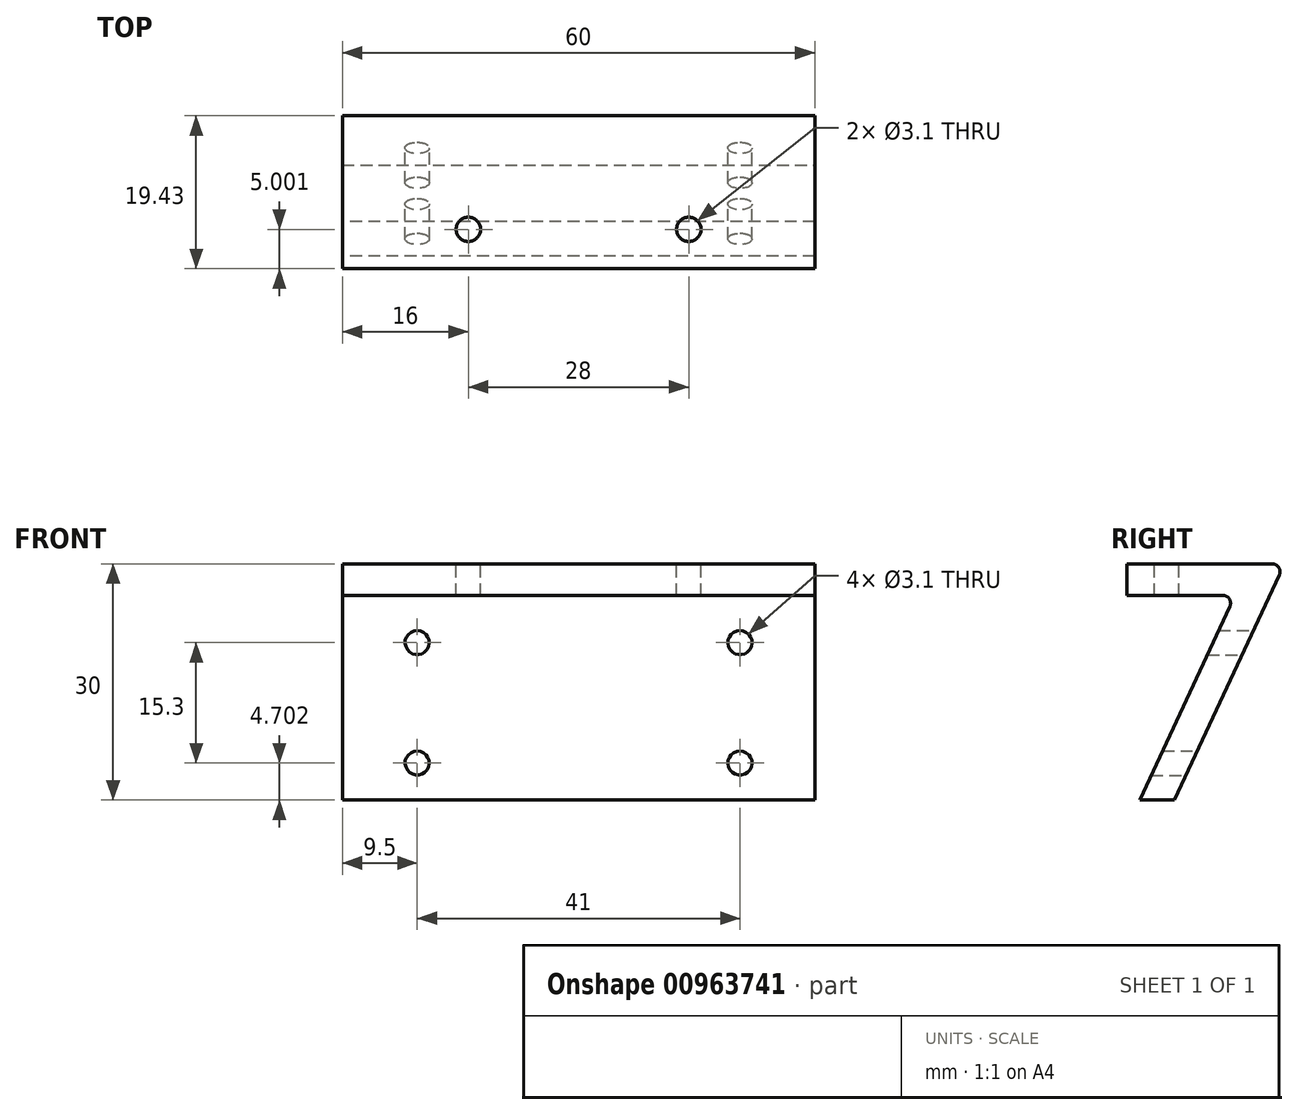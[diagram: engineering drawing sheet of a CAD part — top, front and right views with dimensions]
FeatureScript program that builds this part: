
annotation { "Feature Type Name" : "Feature", "Feature Type Description" : "" }
export const myFeature = defineFeature(function(context is Context, id is Id, definition is map)
    precondition{}
    {
        {
            var Q0;
            Q0=qCreatedBy(makeId("Right.planeOp"),FACE);
            var sketch = newSketch(context, id + "F0", { "sketchPlane" : qUnion([Q0])});
            skLineSegment(sketch, "E0", {"start": v(-23.5, -2.28) * mm, "end": v(-3.5, -2.28) * mm});
            skLineSegment(sketch, "E1", {"start": v(-3.5, -2.28) * mm, "end": v(-17.49, -32.28) * mm});
            skLineSegment(sketch, "E2.0", {"start": v(-9.78, -6.28) * mm, "end": v(-21.9, -32.28) * mm});
            skLineSegment(sketch, "E2.1", {"start": v(-23.5, -6.28) * mm, "end": v(-9.78, -6.28) * mm});
            skLineSegment(sketch, "E3", {"start": v(-23.5, -2.28) * mm, "end": v(-23.5, -6.28) * mm});
            skLineSegment(sketch, "E4", {"start": v(-21.9, -32.28) * mm, "end": v(-17.49, -32.28) * mm});
            skSolve(sketch);
        }
        {
            var Q0;
            Q0=makeQuery(id+"F0.imprint","IMPRINT",FACE,{"disambiguationData":[TD([[makeQuery(id+"F0.imprint","IMPRINT",EDGE,{"derivedFrom":sQuery(id+"F0.wireOp",EDGE,"E0")}),-1.0]])]});
            extrude(context, id + "F1", {"entities" : qUnion([Q0]), "depth" : 60 * mm, "offsetDistance" : 25 * mm});
        }
        {
            var Q0;
            Q0=qCreatedBy(makeId("Top.planeOp"),FACE);
            var sketch = newSketch(context, id + "F2", { "sketchPlane" : qUnion([Q0])});
            skCircle(sketch, "E5", {"center": v(16, -18.5) * mm, "radius": 1.5 * mm});
            skCircle(sketch, "E6", {"center": v(44, -18.5) * mm, "radius": 1.5 * mm});
            skSolve(sketch);
        }
        {
            var Q0;
            Q0=qCreatedBy(makeId("Front.planeOp"),FACE);
            var sketch = newSketch(context, id + "F3", { "sketchPlane" : qUnion([Q0])});
            skCircle(sketch, "E7", {"center": v(9.5, -12.28) * mm, "radius": 1.55 * mm});
            skCircle(sketch, "E8", {"center": v(50.5, -12.28) * mm, "radius": 1.55 * mm});
            skCircle(sketch, "E9", {"center": v(9.5, -27.58) * mm, "radius": 1.55 * mm});
            skCircle(sketch, "E10", {"center": v(50.5, -27.58) * mm, "radius": 1.55 * mm});
            skSolve(sketch);
        }
        {
            var Q0;
            Q0=sQuery(id+"F3.wireOp",VERTEX,"E8.center");
            var Q1;
            Q1=sQuery(id+"F3.wireOp",VERTEX,"E7.center");
            var Q2;
            Q2=sQuery(id+"F3.wireOp",VERTEX,"E9.center");
            var Q3;
            Q3=sQuery(id+"F3.wireOp",VERTEX,"E10.center");
            var Q4;
            Q4=makeQuery(id+"F1.opExtrude","SWEPT_BODY",BODY,{"disambiguationData":[OSD([sQuery(id+"F0.wireOp",EDGE,"E0"),sQuery(id+"F0.wireOp",EDGE,"E1"),sQuery(id+"F0.wireOp",EDGE,"E2.0"),sQuery(id+"F0.wireOp",EDGE,"E2.1"),sQuery(id+"F0.wireOp",EDGE,"E3"),sQuery(id+"F0.wireOp",EDGE,"E4")])]});
            hole(context, id + "F4", {"style" : HoleStyle.SIMPLE, "endStyle" : HoleEndStyle.THROUGH, "oppositeDirection" : true, "holeDiameter" : 3.1 * mm, "majorDiameter" : 5 * mm, "isTappedThrough" : true, "tappedDepth" : 12 * mm, "tapClearance" : 3, "locations" : qUnion([Q0, Q1, Q2, Q3]), "scope" : qUnion([Q4])});
        }
        {
            var Q0;
            Q0=sQuery(id+"F2.wireOp",VERTEX,"E5.center");
            var Q1;
            Q1=sQuery(id+"F2.wireOp",VERTEX,"E6.center");
            var Q2;
            Q2=makeQuery(id+"F1.opExtrude","SWEPT_BODY",BODY,{"disambiguationData":[OSD([sQuery(id+"F0.wireOp",EDGE,"E0"),sQuery(id+"F0.wireOp",EDGE,"E1"),sQuery(id+"F0.wireOp",EDGE,"E2.0"),sQuery(id+"F0.wireOp",EDGE,"E2.1"),sQuery(id+"F0.wireOp",EDGE,"E3"),sQuery(id+"F0.wireOp",EDGE,"E4")])]});
            hole(context, id + "F5", {"style" : HoleStyle.SIMPLE, "endStyle" : HoleEndStyle.BLIND, "holeDiameter" : 3.1 * mm, "majorDiameter" : 5 * mm, "holeDepth" : 12 * mm, "isTappedThrough" : true, "tappedDepth" : 12 * mm, "tapClearance" : 3, "locations" : qUnion([Q0, Q1]), "scope" : qUnion([Q2])});
        }
        {
            var Q0;
            Q0=makeQuery(id+"F1.opExtrude","SWEPT_EDGE",EDGE,{"disambiguationData":[OSD([sQuery(id+"F0.wireOp",EDGE,"E0"),sQuery(id+"F0.wireOp",EDGE,"E1")])]});
            fillet(context, id + "F6", {"entities" : qUnion([Q0]), "radius" : 1 * mm, "tangentPropagation" : true, "allowEdgeOverflow" : false});
        }
        {
            var Q0;
            Q0=makeQuery(id+"F1.opExtrude","SWEPT_EDGE",EDGE,{"disambiguationData":[OSD([sQuery(id+"F0.wireOp",EDGE,"E2.0"),sQuery(id+"F0.wireOp",EDGE,"E2.1")])]});
            fillet(context, id + "F7", {"entities" : qUnion([Q0]), "radius" : 1 * mm, "tangentPropagation" : true, "allowEdgeOverflow" : false});
        }
    });
